# Revit family: ClosetMaid - ShelfTrack EVO - Solid Wood Melamine Walk-In Sample 8x6
name_source: partatom
category: Specialty Equipment
revit_build: Autodesk Revit 2018 (Build: 20190510_1515(x64)
units: mm (PartAtom-declared; Revit-internal decimal feet)

## family parameters
Always vertical = Yes
Cut with Voids When Loaded = No
Part Type = Normal
Room Calculation Point = No
Round Connector Dimension = Use Diameter
Shared = No
Work Plane-Based = No

## types (1)
- 8x6 Sample Walk-In Closet
    Description = 8'x6' Solid Wood Shelving Sample Walk-In Unit
    Drawer Material = White Finish
    Keynote = 10 57 00
    Manufacturer = ClosetMaid
    Number of Brackets = 16
    Number of Shelves = 5
    Number of Standards = 12
    Number of Units = 3
    Shelf Depth = 1' - 2"
    Shelf Material = White Finish
    Standards Length = 7' - 0"
    Support Material = White Finish
    Type Comments = 5/8'' Solid Melamine Shelving
    URL = www.ClosetMaidPro.com

## geometry (parser evidence)
native form markers: Sweep x28
no freeform markers — native parametric forms only
